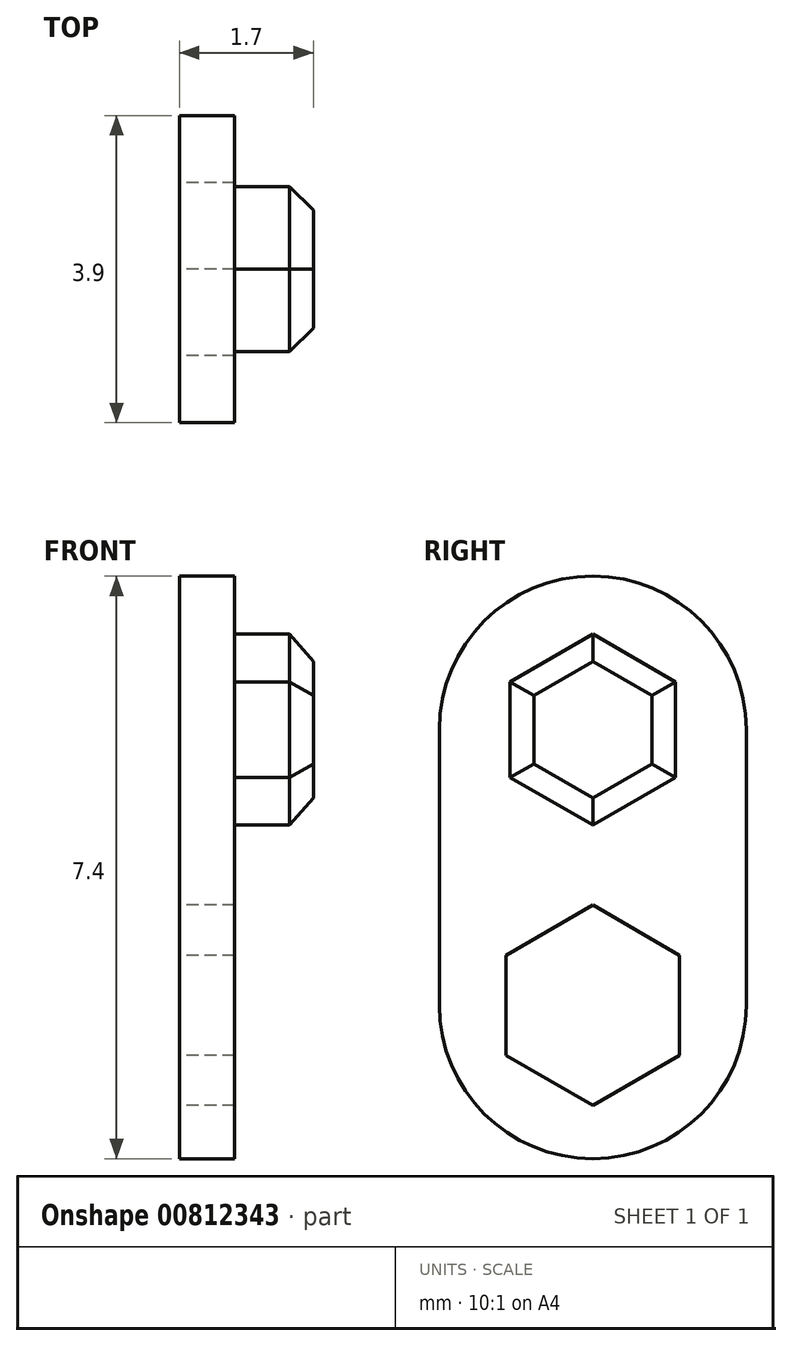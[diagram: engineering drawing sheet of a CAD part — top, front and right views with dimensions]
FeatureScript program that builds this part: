
annotation { "Feature Type Name" : "Feature", "Feature Type Description" : "" }
export const myFeature = defineFeature(function(context is Context, id is Id, definition is map)
    precondition{}
    {
        {
            var Q0;
            Q0=qCreatedBy(makeId("Right.planeOp"),FACE);
            var sketch = newSketch(context, id + "F0", { "sketchPlane" : qUnion([Q0])});
            skLineSegment(sketch, "E0.bottom", {"start": v(1.95, 1.75) * mm, "end": v(-1.95, 1.75) * mm});
            skLineSegment(sketch, "E0.top", {"start": v(1.95, -1.75) * mm, "end": v(-1.95, -1.75) * mm});
            skLineSegment(sketch, "E0.left", {"start": v(1.95, 1.75) * mm, "end": v(1.95, -1.75) * mm});
            skLineSegment(sketch, "E0.right", {"start": v(-1.95, 1.75) * mm, "end": v(-1.95, -1.75) * mm});
            skPoint(sketch, "E0.middle", {"position": v(0, 0) * mm});
            skArc(sketch, "E1", {"start": v(-1.95, 1.75) * mm, "mid": v(0, 3.7) * mm, "end": v(1.95, 1.75) * mm});
            skArc(sketch, "E2", {"start": v(-1.95, -1.75) * mm, "mid": v(0, -3.7) * mm, "end": v(1.95, -1.75) * mm});
            skSolve(sketch);
        }
        {
            var Q0;
            Q0=qSketchRegion(id+"F0",true);
            extrude(context, id + "F1", {"entities" : qUnion([Q0]), "depth" : .7 * mm, "offsetDistance" : 25 * mm});
        }
        {
            var Q0;
            Q0=makeQuery(id+"F1.opExtrude","CAP_FACE",FACE,{"disambiguationData":[OSD([sQuery(id+"F0.wireOp",EDGE,"E0.left"),sQuery(id+"F0.wireOp",EDGE,"E0.right"),sQuery(id+"F0.wireOp",EDGE,"E1"),sQuery(id+"F0.wireOp",EDGE,"E2")])],"isStart":false});
            var sketch = newSketch(context, id + "F2", { "sketchPlane" : qUnion([Q0])});
            skCircle(sketch, "E3.cCircle", {"center": v(0, 1.75) * mm, "radius": 1.05 * mm, "construction": true});
            skLineSegment(sketch, "E3.0", {"start": v(1.05, 2.36) * mm, "end": v(1.05, 1.14) * mm});
            skLineSegment(sketch, "E3.1", {"start": v(1.05, 1.14) * mm, "end": v(0, 0.54) * mm});
            skLineSegment(sketch, "E3.2", {"start": v(0, 0.54) * mm, "end": v(-1.05, 1.14) * mm});
            skLineSegment(sketch, "E3.3", {"start": v(-1.05, 1.14) * mm, "end": v(-1.05, 2.36) * mm});
            skLineSegment(sketch, "E3.4", {"start": v(-1.05, 2.36) * mm, "end": v(0, 2.96) * mm});
            skLineSegment(sketch, "E3.5", {"start": v(0, 2.96) * mm, "end": v(1.05, 2.36) * mm});
            skPoint(sketch, "E3.0.midPoint", {"position": v(1.05, 1.75) * mm});
            skSolve(sketch);
        }
        {
            var Q0;
            Q0=qSketchRegion(id+"F2",true);
            extrude(context, id + "F3", {"entities" : qUnion([Q0]), "operationType" : NewBodyOperationType.ADD, "depth" : 1 * mm, "offsetDistance" : 25 * mm});
        }
        {
            var Q0;
            Q0=makeQuery(id+"F3.opExtrude","CAP_EDGE",EDGE,{"disambiguationData":[OSD([sQuery(id+"F2.wireOp",EDGE,"E3.4")])],"isStart":false});
            var Q1;
            Q1=makeQuery(id+"F3.opExtrude","CAP_EDGE",EDGE,{"disambiguationData":[OSD([sQuery(id+"F2.wireOp",EDGE,"E3.5")])],"isStart":false});
            var Q2;
            Q2=makeQuery(id+"F3.opExtrude","CAP_EDGE",EDGE,{"disambiguationData":[OSD([sQuery(id+"F2.wireOp",EDGE,"E3.0")])],"isStart":false});
            var Q3;
            Q3=makeQuery(id+"F3.opExtrude","CAP_EDGE",EDGE,{"disambiguationData":[OSD([sQuery(id+"F2.wireOp",EDGE,"E3.1")])],"isStart":false});
            var Q4;
            Q4=makeQuery(id+"F3.opExtrude","CAP_EDGE",EDGE,{"disambiguationData":[OSD([sQuery(id+"F2.wireOp",EDGE,"E3.2")])],"isStart":false});
            var Q5;
            Q5=makeQuery(id+"F3.opExtrude","CAP_EDGE",EDGE,{"disambiguationData":[OSD([sQuery(id+"F2.wireOp",EDGE,"E3.3")])],"isStart":false});
            chamfer(context, id + "F4", {"entities" : qUnion([Q0, Q1, Q2, Q3, Q4, Q5]), "width" : .3 * mm, "tangentPropagation" : true});
        }
        {
            var Q0;
            Q0=makeQuery(id+"F1.opExtrude","CAP_FACE",FACE,{"disambiguationData":[OSD([sQuery(id+"F0.wireOp",EDGE,"E0.left"),sQuery(id+"F0.wireOp",EDGE,"E0.right"),sQuery(id+"F0.wireOp",EDGE,"E1"),sQuery(id+"F0.wireOp",EDGE,"E2")])],"isStart":true});
            var sketch = newSketch(context, id + "F5", { "sketchPlane" : qUnion([Q0])});
            skCircle(sketch, "E4.cCircle", {"center": v(0, -1.75) * mm, "radius": 1.1 * mm, "construction": true});
            skLineSegment(sketch, "E4.0", {"start": v(1.1, -1.11) * mm, "end": v(1.1, -2.39) * mm});
            skLineSegment(sketch, "E4.1", {"start": v(1.1, -2.39) * mm, "end": v(0, -3.02) * mm});
            skLineSegment(sketch, "E4.2", {"start": v(0, -3.02) * mm, "end": v(-1.1, -2.39) * mm});
            skLineSegment(sketch, "E4.3", {"start": v(-1.1, -2.39) * mm, "end": v(-1.1, -1.11) * mm});
            skLineSegment(sketch, "E4.4", {"start": v(-1.1, -1.11) * mm, "end": v(0, -0.48) * mm});
            skLineSegment(sketch, "E4.5", {"start": v(0, -0.48) * mm, "end": v(1.1, -1.11) * mm});
            skPoint(sketch, "E4.0.midPoint", {"position": v(1.1, -1.75) * mm});
            skSolve(sketch);
        }
        {
            var Q0;
            Q0=qSketchRegion(id+"F5",true);
            extrude(context, id + "F6", {"entities" : qUnion([Q0]), "operationType" : NewBodyOperationType.REMOVE, "endBound" : BoundingType.UP_TO_NEXT, "oppositeDirection" : true, "depth" : 25 * mm, "offsetDistance" : 25 * mm});
        }
    });
